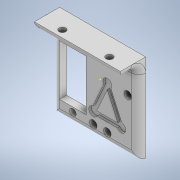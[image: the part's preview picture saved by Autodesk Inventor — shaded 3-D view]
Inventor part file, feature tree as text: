
AUTODESK INVENTOR PART (.ipt)
format: ipt  version: 2022 (Build 260153000, 153)  size: 246,784 bytes
history: native  units: in
note: dims shown in document units (in); Inventor stores cm internally (conversion verified against a paired STEP export)
features: sketch x7, extrude x3, projected_geometry x3, fillet x1
ambient origin geometry x8: Origin, YZ Plane, XZ Plane, XY Plane, X Axis, Y Axis, Z Axis, Center Point
bodies: Solid1 (feature_tree)
feature tree (14):
  extrude  "Extrusion1"  Depth=0.135in
  sketch  "Sketch2"  dims[d2=0.13in d3=0.906in d4=0.48in]
  sketch  "Sketch3"  dims[d5=0.2323in d6=0.084in]
  sketch  "Sketch4"  dims[d7=0.12in]
  extrude  "Extrusion3"  Depth=0.906in
  sketch  "Sketch6"  dims[d9=0.12in]
  fillet  "Fillet2"  Radius=0.48in
  extrude  "Extrusion4"  Depth=0.084in
  sketch  "Sketch1"  dims[d0=0.982in d1=0.135in]
  projected_geometry  "Projected Loop1"
  sketch  "Sketch5"  dims[d8=0.084in]
  projected_geometry  "Projected Loop2"
  sketch  "Sketch7"  dims[d10=0.125in d11=0.125in d12=0.125in d13=0.125in d15=0.125in d16=0.0in d17=0.135in d18=1.425in d19=45.0deg d20=0.295in d21=0.125in d22=0.42in d23=0.12in d26=0.2in d27=0.125in d28=0.42in d29=0.12in d30=0.125in d31=0.0in d33=0.125in d34=0.1575in d35=0.1575in d41=0.0394in d42=0.0394in d43=0.0394in d44=0.0in]
  projected_geometry  "Projected Loop3"
